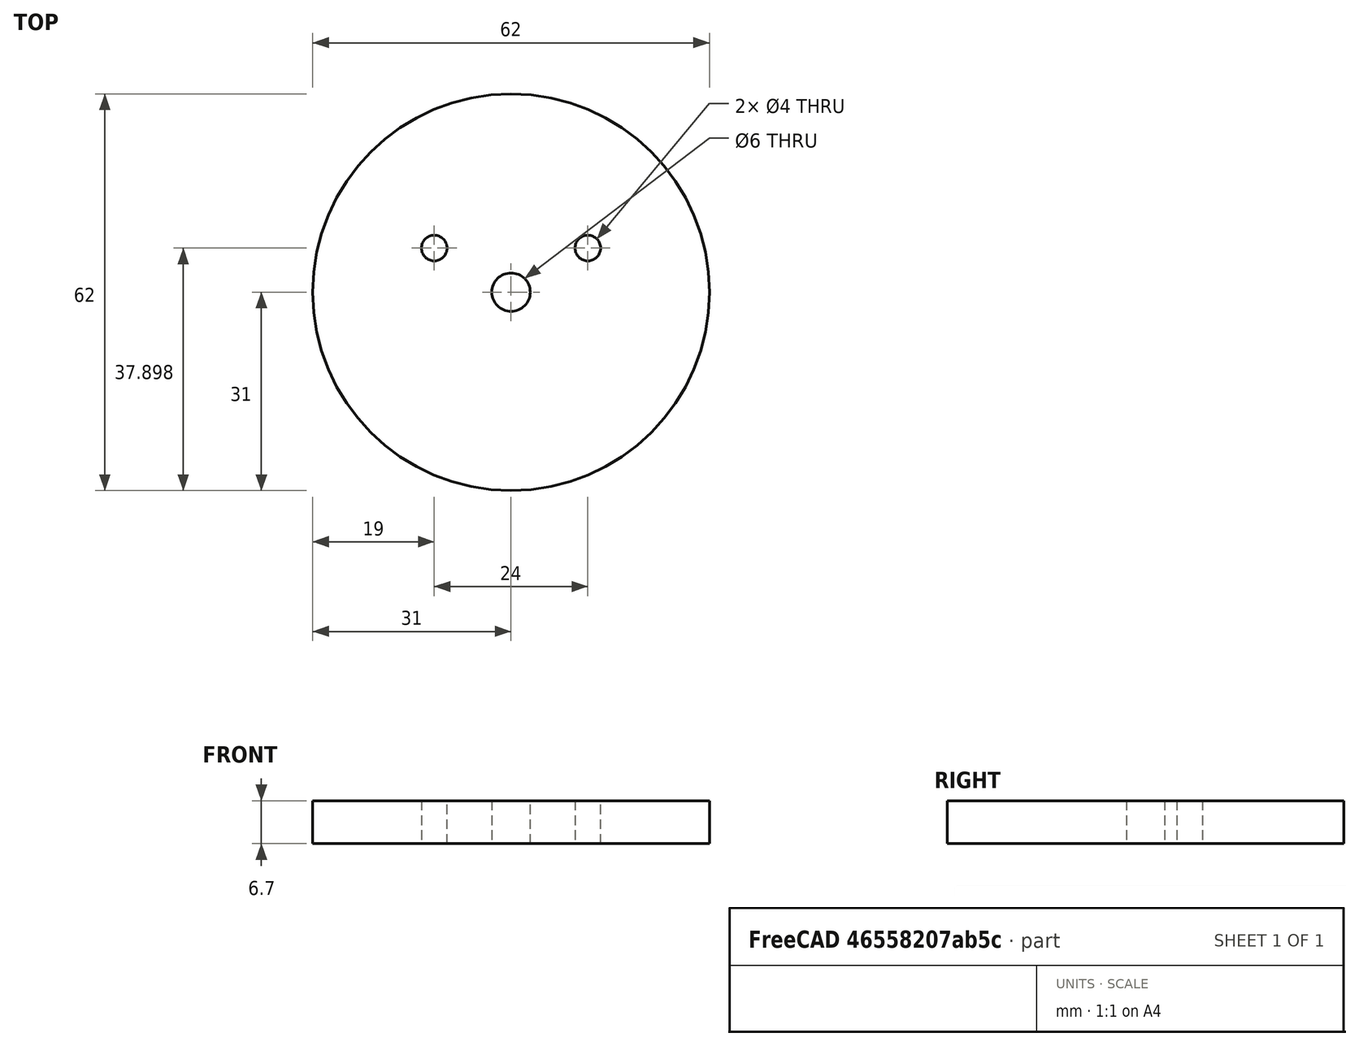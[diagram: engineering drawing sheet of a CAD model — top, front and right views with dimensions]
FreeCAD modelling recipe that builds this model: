
FCSTD DOCUMENT  (FreeCAD 0.18R16093 (Git))
Label: couplerCap_small
License: All rights reserved
LicenseURL: http://en.wikipedia.org/wiki/All_rights_reserved
objects: Sketcher::SketchObject×1, PartDesign::Pad×1, PartDesign::Body×1
note: 4 computed .brp shape members not serialized (recipe doc carries the construction recipe); baked Part::Feature solids carry a one-line shape summary decoded from their .brp

FEATURE [Sketcher::SketchObject] Sketch
  MapMode = 5
  Support = -> [XY_Plane]
  sketch-geometry (4):
    g0: Circle CenterX=0 CenterY=0 CenterZ=0 NormalX=0 NormalY=0 NormalZ=1 AngleXU=0 Radius=31
    g1: Circle CenterX=-12 CenterY=6.89752 CenterZ=0 NormalX=0 NormalY=0 NormalZ=1 AngleXU=0 Radius=2
    g2: Circle CenterX=12 CenterY=6.89752 CenterZ=0 NormalX=0 NormalY=0 NormalZ=1 AngleXU=0 Radius=2
    g3: Circle CenterX=0 CenterY=0 CenterZ=0 NormalX=0 NormalY=0 NormalZ=1 AngleXU=0 Radius=3
  constraints (9):
    c: Coincident(g0,g-1)
    c: Radius(g0) = 31
    c: Horizontal(g1,g2)
    c: Equal(g2,g1)
    c: Radius(g1) = 2
    c: DistanceX(g1,g0) = 12
    c: DistanceX(g0,g2) = 12
    c: Coincident(g3,g0)
    c: Radius(g3) = 3
FEATURE [PartDesign::Pad] Pad
  Length = 6.7
  Length2 = 100
  Profile = -> Sketch
  Type = 0
FEATURE [PartDesign::Body] Body
  Group = -> [Sketch,Pad]
  Origin = -> Origin
  Tip = -> Pad
